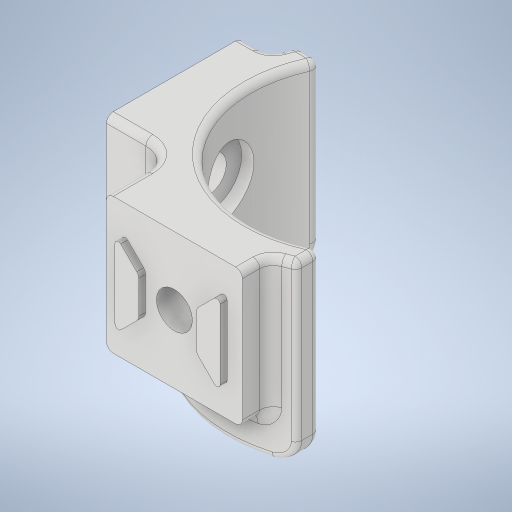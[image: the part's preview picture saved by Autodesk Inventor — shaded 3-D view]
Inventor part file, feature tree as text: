
AUTODESK INVENTOR PART (.ipt)
format: ipt  version: 2024 (Build 280153000, 153)  size: 606,208 bytes
history: native  units: mm
features: sketch x6, plane x5, fillet x5, extrude x3, hole x2, mirror x2, projected_geometry x1
ambient origin geometry x8: Origin, YZ Plane, XZ Plane, XY Plane, X Axis, Y Axis, Z Axis, Center Point
bodies: Body1 (feature_tree)
feature tree (24):
  sketch  "Sketch_66"  dims[d57=0.25mm d58=0.25mm d59=0.25mm d60=0.5mm d61=0.5mm d62=1.0mm d63=1.0mm d64=0.0mm d68=-4.0mm d87=-5.0mm d92=15.0mm d106=42.0mm d107=8.0mm d108=3.0mm d109=3.0mm d110=6.0mm d111=20.0mm d112=0.0mm d113=1.0mm d114=2.0mm d115=3.0mm d116=1.0mm d117=1.0mm d34=0.5mm d35=0.872665mm d36=0.5mm d37=0.872665mm d88=0.872665mm d89=0.5mm d90=0.872665mm d91=0.0mm d93=0.0mm]
  sketch  "Sketch3"  dims[d14=20.0mm d15=20.0mm]
  extrude  "Extrusion2"  Depth=20.0mm
  plane  "Work Plane6"
  plane  "Work Plane8"
  plane  "Work Plane9"
  extrude  "Extrusion9"  Depth=20.0mm
  fillet  "Fillet14"  Radius=9.8mm
  fillet  "Fillet15"  Radius=9.8mm
  fillet  "Fillet16"  Radius=4.5mm
  fillet  "Fillet17"  Radius=4.5mm
  fillet  "Fillet18"  Radius=35.0mm
  hole  "Hole3"  [1 undecoded]
  plane  "Work Plane4"
  hole  "Hole4"  [1 undecoded]
  extrude  "Extrusion4"  Depth=0.5mm
  mirror  "Mirror1"
  plane  "Work Plane7"
  mirror  "Mirror3"
  sketch  "Sketch6"  dims[d16=20.0mm d17=20.0mm d18=9.8mm d19=9.8mm d20=4.5mm d21=4.5mm d22=35.0mm]
  sketch  "Sketch7"  dims[d23=20.0mm d24=0.0mm]
  sketch  "Sketch8"  dims[d41=5.3mm d42=6.0mm d43=4.0mm d44=2.0mm d45=90.0deg d46=8.0mm d47=20.594885mm d48=-5.0mm]
  sketch  "Sketch13"  dims[d49=9.8mm d50=6.0mm d51=4.0mm d52=2.0mm d53=90.0deg d54=8.0mm d55=20.594885mm d56=0.25mm]
  projected_geometry  "Projected Loop3"
note: 2 required parameter values undecoded (feature->parameter linkage not recoverable at this tier; creation-order binding heuristic only, values carry confidence <= 0.55)
